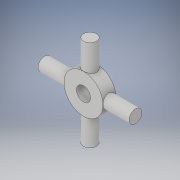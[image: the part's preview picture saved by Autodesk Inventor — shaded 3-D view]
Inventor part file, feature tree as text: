
AUTODESK INVENTOR PART (.ipt)
format: ipt  version: 2019 (Build 230136000, 136)  size: 136,704 bytes
history: native  units: in
note: dims shown in document units (in); Inventor stores cm internally (conversion verified against a paired STEP export)
features: sketch x5, extrude x2, pattern_circular x1, hole x1, plane x1
ambient origin geometry x8: Origin, YZ Plane, XZ Plane, XY Plane, X Axis, Y Axis, Z Axis, Center Point
bodies: Solid1 (feature_tree)
feature tree (10):
  extrude  "Extrusion1"  Depth=0.25in TaperAngle=0.0deg
  pattern_circular  "Circular Pattern1"  Count=4 Angle=360.0deg
  extrude  "Extrusion2"  Depth=0.25in TaperAngle=0.0deg
  hole  "Hole1"  [1 undecoded]
  sketch  "Sketch4"
  plane  "Work Plane1"
  sketch  "Sketch5"
  sketch  "Sketch1"  dims[d0=0.25in d1=0.875in d2=0.0in d3=1.5748in d4=360.0deg]
  sketch  "Sketch2"  dims[d6=0.75in d7=0.25in d8=0.0in]
  sketch  "Sketch3"  dims[d9=0.27in d10=0.75in d11=0.375in d12=0.25in d13=0.5635in d14=1.0in d15=0.8108in d16=45.0deg]
note: 1 required parameter value undecoded (feature->parameter linkage not recoverable at this tier; creation-order binding heuristic only, values carry confidence <= 0.55)
